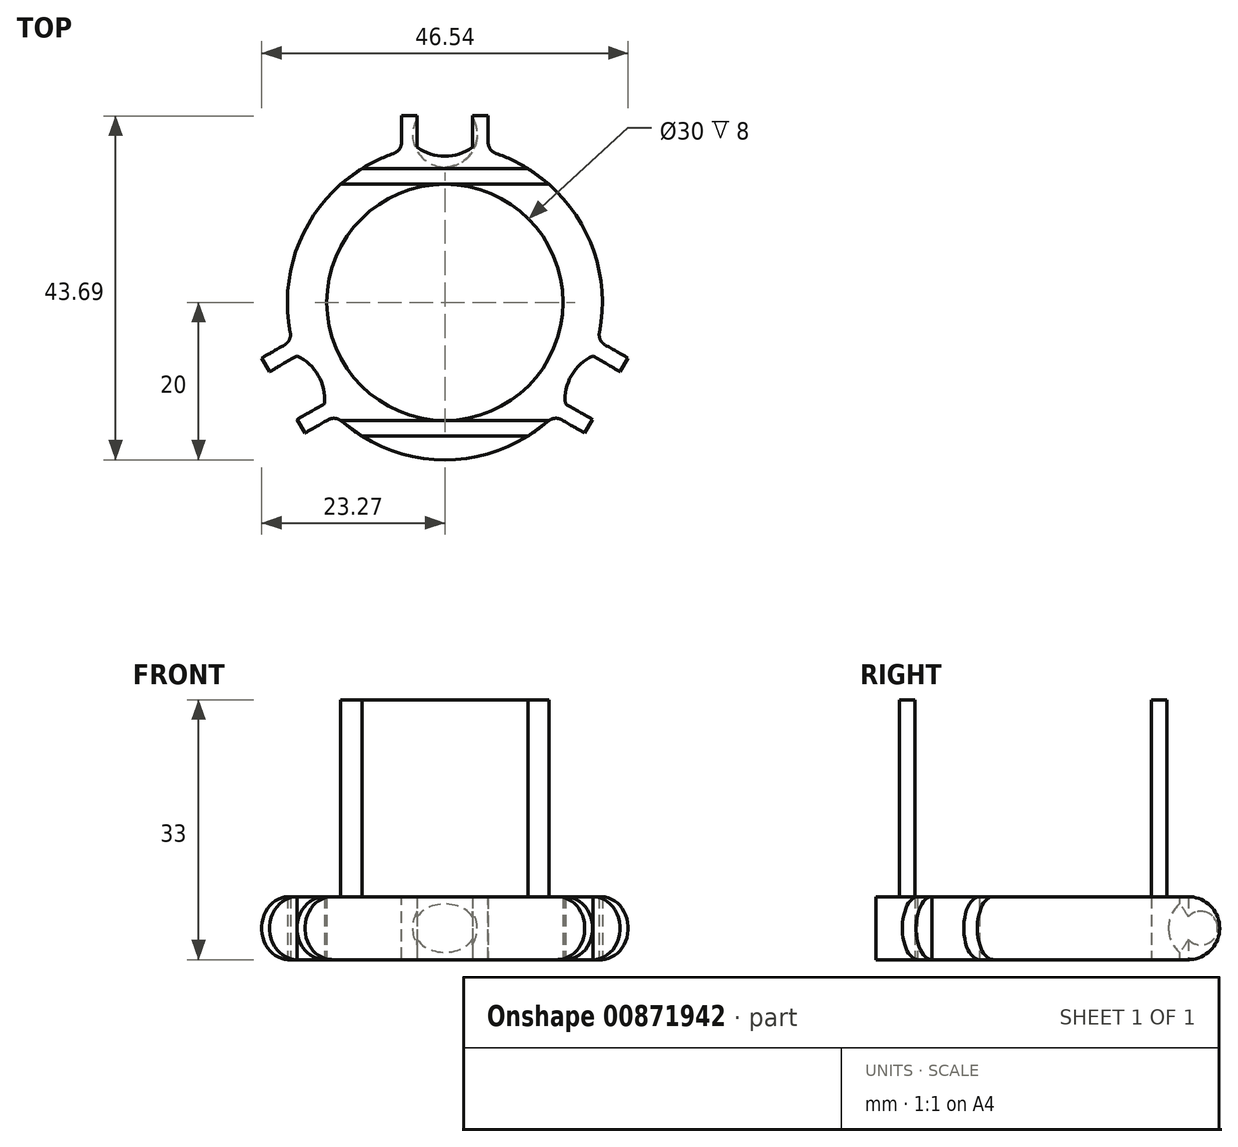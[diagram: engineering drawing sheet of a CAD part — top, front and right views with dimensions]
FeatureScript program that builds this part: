
annotation { "Feature Type Name" : "Feature", "Feature Type Description" : "" }
export const myFeature = defineFeature(function(context is Context, id is Id, definition is map)
    precondition{}
    {
        {
            var Q0;
            Q0=qCreatedBy(makeId("Top.planeOp"),FACE);
            var sketch = newSketch(context, id + "F0", { "sketchPlane" : qUnion([Q0])});
            skArc(sketch, "E0", {"start": v(-5.5, 19.23) * mm, "mid": v(-17.32, 10) * mm, "end": v(-19.4, -4.85) * mm});
            skLineSegment(sketch, "E1", {"start": v(0, 23.66) * mm, "end": v(0, -22.84) * mm, "construction": true});
            skLineSegment(sketch, "E2", {"start": v(-22.74, 0) * mm, "end": v(26.82, 0) * mm, "construction": true});
            skLineSegment(sketch, "E3", {"start": v(-3.5, 19.7) * mm, "end": v(-3.5, 23.7) * mm});
            skLineSegment(sketch, "E4", {"start": v(-3.5, 23.7) * mm, "end": v(-5.5, 23.7) * mm});
            skLineSegment(sketch, "E5", {"start": v(-5.5, 23.7) * mm, "end": v(-5.5, 19.23) * mm});
            skLineSegment(sketch, "E6.MirrorCS", {"start": v(3.5, 19.7) * mm, "end": v(3.5, 23.7) * mm});
            skLineSegment(sketch, "E7.MirrorCS", {"start": v(3.5, 23.7) * mm, "end": v(5.5, 23.7) * mm});
            skLineSegment(sketch, "E8.MirrorCS", {"start": v(5.5, 23.7) * mm, "end": v(5.5, 19.23) * mm});
            skLineSegment(sketch, "E9", {"start": v(-3.5, 19.7) * mm, "end": v(3.5, 19.7) * mm, "construction": true});
            skLineSegment(sketch, "E10", {"start": v(-3.5, 23.7) * mm, "end": v(3.5, 23.7) * mm, "construction": true});
            skPoint(sketch, "E11", {"position": v(0, 9.18) * mm});
            skLineSegment(sketch, "E12.1.0", {"start": v(-17.77, -16.6) * mm, "end": v(-13.9, -14.38) * mm});
            skLineSegment(sketch, "E12.1.1", {"start": v(-18.77, -14.88) * mm, "end": v(-17.77, -16.6) * mm});
            skLineSegment(sketch, "E12.1.2", {"start": v(-18.8, -6.81) * mm, "end": v(-22.27, -8.81) * mm});
            skLineSegment(sketch, "E12.1.3", {"start": v(-22.27, -8.81) * mm, "end": v(-23.27, -7.08) * mm});
            skLineSegment(sketch, "E12.1.4", {"start": v(-23.27, -7.08) * mm, "end": v(-19.4, -4.85) * mm});
            skLineSegment(sketch, "E12.1.5", {"start": v(-15.3, -12.88) * mm, "end": v(-18.77, -14.88) * mm});
            skLineSegment(sketch, "E12.2.0", {"start": v(23.27, -7.08) * mm, "end": v(19.4, -4.85) * mm});
            skLineSegment(sketch, "E12.2.1", {"start": v(22.27, -8.81) * mm, "end": v(23.27, -7.08) * mm});
            skLineSegment(sketch, "E12.2.2", {"start": v(15.3, -12.88) * mm, "end": v(18.77, -14.88) * mm});
            skLineSegment(sketch, "E12.2.3", {"start": v(18.77, -14.88) * mm, "end": v(17.77, -16.6) * mm});
            skLineSegment(sketch, "E12.2.4", {"start": v(17.77, -16.6) * mm, "end": v(13.9, -14.38) * mm});
            skLineSegment(sketch, "E12.2.5", {"start": v(18.8, -6.81) * mm, "end": v(22.27, -8.81) * mm});
            skArc(sketch, "E13.trimOffspring", {"start": v(19.4, -4.85) * mm, "mid": v(17.32, 10) * mm, "end": v(5.5, 19.23) * mm});
            skArc(sketch, "E14.trimOffspring", {"start": v(-13.9, -14.38) * mm, "mid": v(0, -20) * mm, "end": v(13.9, -14.38) * mm});
            skCircle(sketch, "E15", {"center": v(0, 0) * mm, "radius": 15 * mm});
            skArc(sketch, "E16", {"start": v(-3.5, 19.7) * mm, "mid": v(0, 18.56) * mm, "end": v(3.5, 19.7) * mm});
            skArc(sketch, "E17.1.0", {"start": v(-15.3, -12.88) * mm, "mid": v(-16.08, -9.28) * mm, "end": v(-18.8, -6.81) * mm});
            skArc(sketch, "E17.2.0", {"start": v(18.8, -6.81) * mm, "mid": v(16.08, -9.28) * mm, "end": v(15.3, -12.88) * mm});
            skSolve(sketch);
        }
        {
            var Q0;
            Q0=qCreatedBy(makeId("Front.planeOp"),FACE);
            var sketch = newSketch(context, id + "F1", { "sketchPlane" : qUnion([Q0])});
            skLineSegment(sketch, "E18", {"start": v(0, -15.32) * mm, "end": v(0, 34.97) * mm, "construction": true});
            skSolve(sketch);
        }
        {
            var Q0;
            Q0=qSketchRegion(id+"F0",true);
            extrude(context, id + "F2", {"entities" : qUnion([Q0]), "depth" : 8 * mm, "offsetDistance" : 25 * mm});
        }
        {
            var Q0;
            Q0=qCreatedBy(makeId("Top.planeOp"),FACE);
            cPlane(context, id + "F3", {"entities" : qUnion([Q0]), "cplaneType" : CPlaneType.OFFSET, "offset" : 4 * mm, "width" : 150 * mm, "height" : 150 * mm});
        }
        {
            var Q0;
            Q0=qCreatedBy(id+"F3.planeOp",FACE);
            var sketch = newSketch(context, id + "F4", { "sketchPlane" : qUnion([Q0])});
            skPoint(sketch, "E19.0", {"position": v(-3.5, 23.7) * mm});
            skPoint(sketch, "E20.0", {"position": v(3.5, 23.7) * mm});
            skLineSegment(sketch, "E21", {"start": v(0, 25.4) * mm, "end": v(0, 17.2) * mm});
            skArc(sketch, "E22", {"start": v(0, 25.4) * mm, "mid": v(-4.1, 21.3) * mm, "end": v(0, 17.2) * mm});
            skLineSegment(sketch, "E23", {"start": v(-3.5, 23.7) * mm, "end": v(3.5, 23.7) * mm, "construction": true});
            skLineSegment(sketch, "E24", {"start": v(0, 29.78) * mm, "end": v(0, 25.4) * mm, "construction": true});
            skPoint(sketch, "E25", {"position": v(0, 25.4) * mm});
            skSolve(sketch);
        }
        {
            var Q0;
            Q0=qSketchRegion(id+"F4",true);
            var Q1;
            Q1=sQuery(id+"F4.wireOp",EDGE,"E21");
            revolve(context, id + "F5", {"operationType" : NewBodyOperationType.REMOVE, "surfaceOperationType" : NewSurfaceOperationType.NEW, "entities" : qUnion([Q0]), "axis" : qUnion([Q1]), "revolveType" : RevolveType.FULL, "oppositeDirection" : true});
        }
        {
            var Q0;
            Q0=makeQuery(id+"F2.opExtrude","CAP_EDGE",EDGE,{"disambiguationData":[OSD([sQuery(id+"F0.wireOp",EDGE,"E4")])],"isStart":false});
            var Q1;
            Q1=makeQuery(id+"F2.opExtrude","CAP_EDGE",EDGE,{"disambiguationData":[OSD([sQuery(id+"F0.wireOp",EDGE,"E7.MirrorCS")])],"isStart":false});
            var Q2;
            Q2=makeQuery(id+"F2.opExtrude","CAP_EDGE",EDGE,{"disambiguationData":[OSD([sQuery(id+"F0.wireOp",EDGE,"E12.2.1")])],"isStart":false});
            var Q3;
            Q3=makeQuery(id+"F2.opExtrude","CAP_EDGE",EDGE,{"disambiguationData":[OSD([sQuery(id+"F0.wireOp",EDGE,"E12.2.3")])],"isStart":false});
            var Q4;
            Q4=makeQuery(id+"F2.opExtrude","CAP_EDGE",EDGE,{"disambiguationData":[OSD([sQuery(id+"F0.wireOp",EDGE,"E12.1.1")])],"isStart":false});
            var Q5;
            Q5=makeQuery(id+"F2.opExtrude","CAP_EDGE",EDGE,{"disambiguationData":[OSD([sQuery(id+"F0.wireOp",EDGE,"E12.1.3")])],"isStart":false});
            var Q6;
            Q6=makeQuery(id+"F2.opExtrude","CAP_EDGE",EDGE,{"disambiguationData":[OSD([sQuery(id+"F0.wireOp",EDGE,"E12.1.1")])],"isStart":true});
            var Q7;
            Q7=makeQuery(id+"F2.opExtrude","CAP_EDGE",EDGE,{"disambiguationData":[OSD([sQuery(id+"F0.wireOp",EDGE,"E12.1.3")])],"isStart":true});
            var Q8;
            Q8=makeQuery(id+"F2.opExtrude","CAP_EDGE",EDGE,{"disambiguationData":[OSD([sQuery(id+"F0.wireOp",EDGE,"E12.2.3")])],"isStart":true});
            var Q9;
            Q9=makeQuery(id+"F2.opExtrude","CAP_EDGE",EDGE,{"disambiguationData":[OSD([sQuery(id+"F0.wireOp",EDGE,"E12.2.1")])],"isStart":true});
            var Q10;
            Q10=makeQuery(id+"F2.opExtrude","CAP_EDGE",EDGE,{"disambiguationData":[OSD([sQuery(id+"F0.wireOp",EDGE,"E7.MirrorCS")])],"isStart":true});
            var Q11;
            Q11=makeQuery(id+"F2.opExtrude","CAP_EDGE",EDGE,{"disambiguationData":[OSD([sQuery(id+"F0.wireOp",EDGE,"E4")])],"isStart":true});
            fillet(context, id + "F6", {"entities" : qUnion([Q0, Q1, Q2, Q3, Q4, Q5, Q6, Q7, Q8, Q9, Q10, Q11]), "radius" : 4 * mm, "tangentPropagation" : true, "allowEdgeOverflow" : false});
        }
        {
            var Q0;
            Q0=makeQuery(id+"F2.opExtrude","SWEPT_EDGE",EDGE,{"disambiguationData":[OSD([sQuery(id+"F0.wireOp",EDGE,"E0"),sQuery(id+"F0.wireOp",EDGE,"E12.1.4")])]});
            var Q1;
            Q1=makeQuery(id+"F2.opExtrude","SWEPT_EDGE",EDGE,{"disambiguationData":[OSD([sQuery(id+"F0.wireOp",EDGE,"E0"),sQuery(id+"F0.wireOp",EDGE,"E5")])]});
            var Q2;
            Q2=makeQuery(id+"F2.opExtrude","SWEPT_EDGE",EDGE,{"disambiguationData":[OSD([sQuery(id+"F0.wireOp",EDGE,"E8.MirrorCS"),sQuery(id+"F0.wireOp",EDGE,"E13.trimOffspring")])]});
            var Q3;
            Q3=makeQuery(id+"F2.opExtrude","SWEPT_EDGE",EDGE,{"disambiguationData":[OSD([sQuery(id+"F0.wireOp",EDGE,"E12.2.0"),sQuery(id+"F0.wireOp",EDGE,"E13.trimOffspring")])]});
            var Q4;
            Q4=makeQuery(id+"F2.opExtrude","SWEPT_EDGE",EDGE,{"disambiguationData":[OSD([sQuery(id+"F0.wireOp",EDGE,"E12.2.4"),sQuery(id+"F0.wireOp",EDGE,"E14.trimOffspring")])]});
            var Q5;
            Q5=makeQuery(id+"F2.opExtrude","SWEPT_EDGE",EDGE,{"disambiguationData":[OSD([sQuery(id+"F0.wireOp",EDGE,"E12.1.0"),sQuery(id+"F0.wireOp",EDGE,"E14.trimOffspring")])]});
            fillet(context, id + "F7", {"entities" : qUnion([Q0, Q1, Q2, Q3, Q4, Q5]), "radius" : 1.5 * mm, "tangentPropagation" : true, "allowEdgeOverflow" : false});
        }
        {
            var Q0;
            Q0=makeQuery(id+"F2.opExtrude","CAP_FACE",FACE,{"disambiguationData":[OSD([sQuery(id+"F0.wireOp",EDGE,"E0"),sQuery(id+"F0.wireOp",EDGE,"E3"),sQuery(id+"F0.wireOp",EDGE,"E4"),sQuery(id+"F0.wireOp",EDGE,"E5"),sQuery(id+"F0.wireOp",EDGE,"E6.MirrorCS"),sQuery(id+"F0.wireOp",EDGE,"E7.MirrorCS"),sQuery(id+"F0.wireOp",EDGE,"E8.MirrorCS"),sQuery(id+"F0.wireOp",EDGE,"E12.1.0"),sQuery(id+"F0.wireOp",EDGE,"E12.1.1"),sQuery(id+"F0.wireOp",EDGE,"E12.1.2"),sQuery(id+"F0.wireOp",EDGE,"E12.1.3"),sQuery(id+"F0.wireOp",EDGE,"E12.1.4"),sQuery(id+"F0.wireOp",EDGE,"E12.1.5"),sQuery(id+"F0.wireOp",EDGE,"E12.2.0"),sQuery(id+"F0.wireOp",EDGE,"E12.2.1"),sQuery(id+"F0.wireOp",EDGE,"E12.2.2"),sQuery(id+"F0.wireOp",EDGE,"E12.2.3"),sQuery(id+"F0.wireOp",EDGE,"E12.2.4"),sQuery(id+"F0.wireOp",EDGE,"E12.2.5"),sQuery(id+"F0.wireOp",EDGE,"E13.trimOffspring"),sQuery(id+"F0.wireOp",EDGE,"E14.trimOffspring"),sQuery(id+"F0.wireOp",EDGE,"E15"),sQuery(id+"F0.wireOp",EDGE,"E16"),sQuery(id+"F0.wireOp",EDGE,"E17.1.0"),sQuery(id+"F0.wireOp",EDGE,"E17.2.0")])],"isStart":false});
            var sketch = newSketch(context, id + "F8", { "sketchPlane" : qUnion([Q0])});
            skLineSegment(sketch, "E26", {"start": v(15, 19.99) * mm, "end": v(15, -27.7) * mm, "construction": true});
            skLineSegment(sketch, "E27", {"start": v(0, 29.52) * mm, "end": v(0, -30.44) * mm, "construction": true});
            skLineSegment(sketch, "E28.MirrorCS", {"start": v(-15, 19.99) * mm, "end": v(-15, -27.7) * mm, "construction": true});
            skLineSegment(sketch, "E29", {"start": v(-29.46, 0) * mm, "end": v(28.93, 0) * mm, "construction": true});
            skLineSegment(sketch, "E30", {"start": v(-13.23, 15) * mm, "end": v(13.23, 15) * mm});
            skLineSegment(sketch, "E31", {"start": v(-10.54, 17) * mm, "end": v(10.54, 17) * mm});
            skLineSegment(sketch, "E32", {"start": v(-10.54, 17) * mm, "end": v(-13.23, 15) * mm});
            skLineSegment(sketch, "E33", {"start": v(10.54, 17) * mm, "end": v(13.23, 15) * mm});
            skLineSegment(sketch, "E34.MirrorCS", {"start": v(-13.23, -15) * mm, "end": v(13.23, -15) * mm});
            skLineSegment(sketch, "E35.MirrorCS", {"start": v(-10.54, -17) * mm, "end": v(-13.23, -15) * mm});
            skLineSegment(sketch, "E36.MirrorCS", {"start": v(-10.54, -17) * mm, "end": v(10.54, -17) * mm});
            skLineSegment(sketch, "E37.MirrorCS", {"start": v(10.54, -17) * mm, "end": v(13.23, -15) * mm});
            skSolve(sketch);
        }
        {
            var Q0;
            Q0=makeQuery(id+"F8.imprint","IMPRINT",FACE,{"disambiguationData":[TD([[makeQuery(id+"F8.imprint","IMPRINT",EDGE,{"derivedFrom":sQuery(id+"F8.wireOp",EDGE,"E31")}),-1.0]])]});
            var Q1;
            {var subQ0=sQuery(id+"F8.wireOp",EDGE,"E35.MirrorCS");Q1=makeQuery(id+"F8.imprint","IMPRINT",FACE,{"disambiguationData":[TD([[makeQuery(id+"F8.imprint","IMPRINT",EDGE,{"derivedFrom":subQ0}),-1.0]])]});}
            extrude(context, id + "F9", {"entities" : qUnion([Q0, Q1]), "operationType" : NewBodyOperationType.ADD, "depth" : 25 * mm, "offsetDistance" : 25 * mm});
        }
    });
